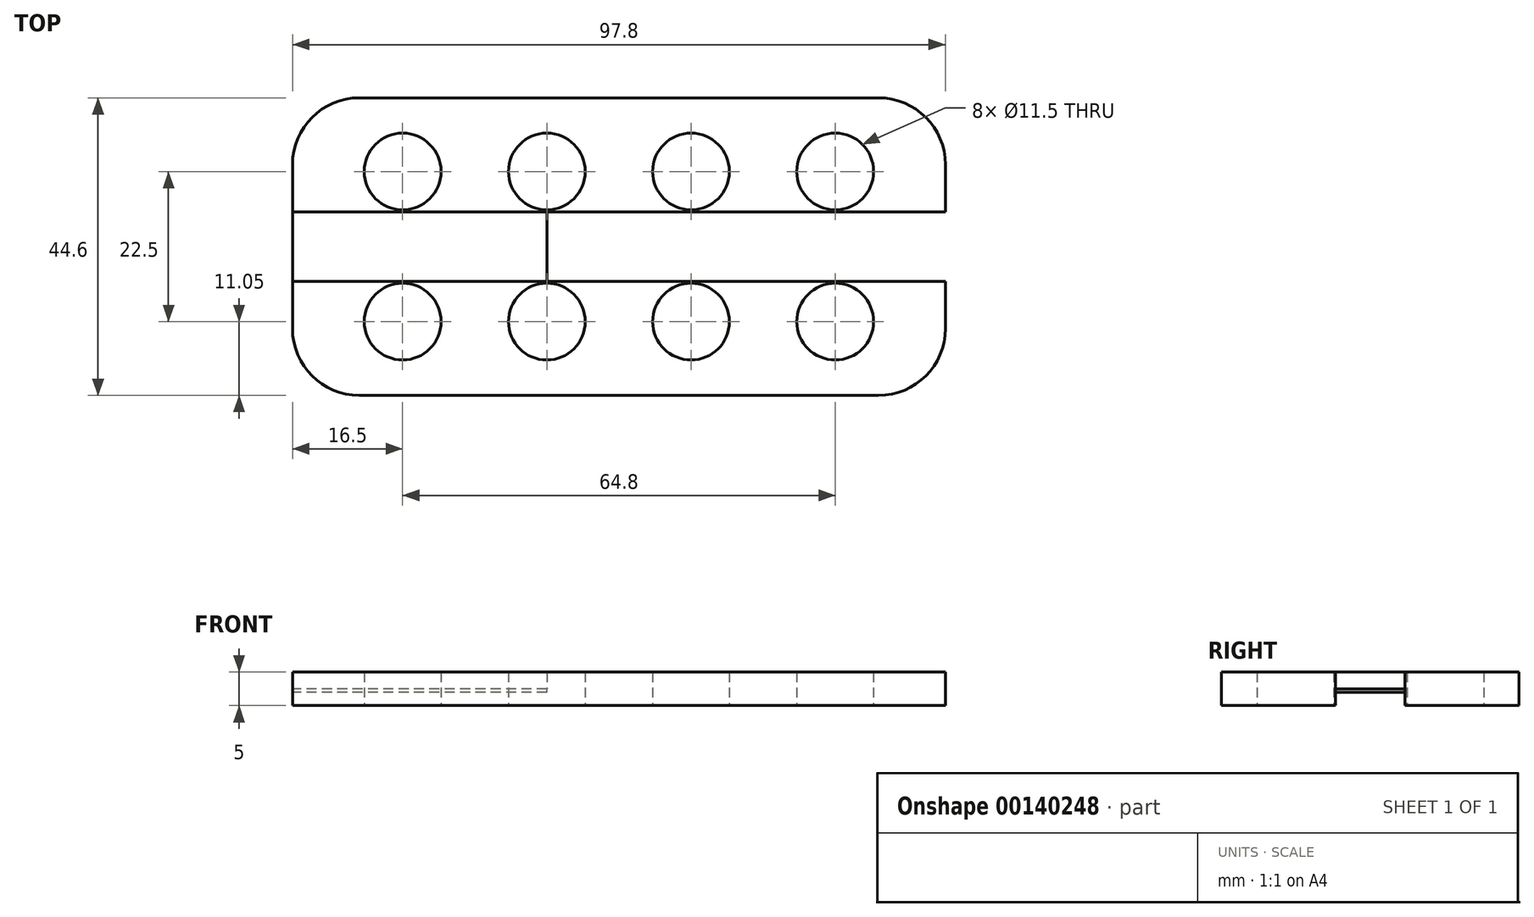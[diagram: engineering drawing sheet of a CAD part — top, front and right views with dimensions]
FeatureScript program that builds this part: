
annotation { "Feature Type Name" : "Feature", "Feature Type Description" : "" }
export const myFeature = defineFeature(function(context is Context, id is Id, definition is map)
    precondition{}
    {
        {
            var Q0;
            Q0=qCreatedBy(makeId("Top.planeOp"),FACE);
            var sketch = newSketch(context, id + "F0", { "sketchPlane" : qUnion([Q0])});
            skLineSegment(sketch, "E0", {"start": v(-3.6, 0) * mm, "end": v(-3.6, 10.25) * mm});
            skLineSegment(sketch, "E1", {"start": v(-3.6, 10.25) * mm, "end": v(18, 10.25) * mm});
            skLineSegment(sketch, "E2", {"start": v(-3.6, 10.25) * mm, "end": v(-25.2, 10.25) * mm});
            skLineSegment(sketch, "E3", {"start": v(-3.6, 0) * mm, "end": v(-3.6, -10.25) * mm});
            skLineSegment(sketch, "E4", {"start": v(-3.6, -10.25) * mm, "end": v(-25.2, -10.25) * mm});
            skLineSegment(sketch, "E5", {"start": v(-3.6, -10.25) * mm, "end": v(18, -10.25) * mm});
            skLineSegment(sketch, "E6.0", {"start": v(-3.6, 11.25) * mm, "end": v(-25.2, 11.25) * mm});
            skLineSegment(sketch, "E6.1", {"start": v(-3.6, 11.25) * mm, "end": v(18, 11.25) * mm});
            skLineSegment(sketch, "E7.0", {"start": v(-3.6, -11.25) * mm, "end": v(18, -11.25) * mm});
            skLineSegment(sketch, "E7.1", {"start": v(-3.6, -11.25) * mm, "end": v(-25.2, -11.25) * mm});
            skLineSegment(sketch, "E8", {"start": v(18, -11.25) * mm, "end": v(39.6, -11.25) * mm});
            skLineSegment(sketch, "E9", {"start": v(18, 11.25) * mm, "end": v(39.6, 11.25) * mm});
            skLineSegment(sketch, "E10", {"start": v(7.2, 11.25) * mm, "end": v(7.2, 0) * mm});
            skLineSegment(sketch, "E11.bottom", {"start": v(-41.7, 22.3) * mm, "end": v(56.1, 22.3) * mm});
            skLineSegment(sketch, "E11.top", {"start": v(-41.7, -22.3) * mm, "end": v(56.1, -22.3) * mm});
            skLineSegment(sketch, "E11.left", {"start": v(-41.7, 22.3) * mm, "end": v(-41.7, -22.3) * mm});
            skLineSegment(sketch, "E11.right", {"start": v(56.1, 22.3) * mm, "end": v(56.1, -22.3) * mm});
            skPoint(sketch, "E11.middle", {"position": v(7.2, 0) * mm});
            skCircle(sketch, "E12", {"center": v(-25.2, 11.25) * mm, "radius": 5.75 * mm});
            skCircle(sketch, "E13", {"center": v(-3.6, 11.25) * mm, "radius": 5.75 * mm});
            skCircle(sketch, "E14", {"center": v(18, 11.25) * mm, "radius": 5.75 * mm});
            skCircle(sketch, "E15", {"center": v(39.6, 11.25) * mm, "radius": 5.75 * mm});
            skCircle(sketch, "E16", {"center": v(-25.2, -11.25) * mm, "radius": 5.75 * mm});
            skCircle(sketch, "E17", {"center": v(-3.6, -11.25) * mm, "radius": 5.75 * mm});
            skCircle(sketch, "E18", {"center": v(18, -11.25) * mm, "radius": 5.75 * mm});
            skCircle(sketch, "E19", {"center": v(39.6, -11.25) * mm, "radius": 5.75 * mm});
            skLineSegment(sketch, "E20", {"start": v(56.1, 0) * mm, "end": v(56.1, -5.2) * mm});
            skLineSegment(sketch, "E21", {"start": v(56.1, 0) * mm, "end": v(56.1, 5.2) * mm});
            skLineSegment(sketch, "E22", {"start": v(56.1, 5.2) * mm, "end": v(-41.7, 5.2) * mm});
            skLineSegment(sketch, "E23", {"start": v(56.1, -5.2) * mm, "end": v(-41.7, -5.2) * mm});
            skSolve(sketch);
        }
        {
            var Q0;
            Q0=makeQuery(id+"F0.imprint","IMPRINT",FACE,{"disambiguationData":[TD([[makeQuery(id+"F0.imprint","IMPRINT",EDGE,{"derivedFrom":sQuery(id+"F0.wireOp",EDGE,"E11.bottom")}),-1.0]])]});
            var Q1;
            {var subQ0=sQuery(id+"F0.wireOp",EDGE,"f6887ee9-049f-47f7-8b07-7ff9263f95ff");var subQ1=makeQuery(id+"F0.imprint","INTERSECT",VERTEX,{"derivedFrom":[sQuery(id+"F0.wireOp",EDGE,"E4"),subQ0]});Q1=makeQuery(id+"F0.imprint","IMPRINT",FACE,{"disambiguationData":[TD([[makeQuery(id+"F0.imprint","IMPRINT",EDGE,{"disambiguationData":[TD([[subQ1,-1.0]])],"derivedFrom":subQ0}),1.0]])]});}
            var Q2;
            {var subQ0=sQuery(id+"F0.wireOp",EDGE,"7b2065db-7b24-4620-b89c-c6dd7d309109");var subQ1=makeQuery(id+"F0.imprint","INTERSECT",VERTEX,{"derivedFrom":[sQuery(id+"F0.wireOp",EDGE,"E2"),subQ0]});Q2=makeQuery(id+"F0.imprint","IMPRINT",FACE,{"disambiguationData":[TD([[makeQuery(id+"F0.imprint","IMPRINT",EDGE,{"disambiguationData":[TD([[subQ1,-1.0]])],"derivedFrom":subQ0}),1.0]])]});}
            var Q3;
            {var subQ1=sQuery(id+"F0.wireOp",EDGE,"E0");var subQ3=sQuery(id+"F0.wireOp",EDGE,"3ee279bb-5b09-4dd3-93a1-242deb24ec6a");var subQ4=makeQuery(id+"F0.imprint","INTERSECT",VERTEX,{"derivedFrom":[subQ1,subQ3]});Q3=makeQuery(id+"F0.imprint","IMPRINT",FACE,{"disambiguationData":[TD([[makeQuery(id+"F0.imprint","IMPRINT",EDGE,{"disambiguationData":[TD([[subQ4,1.0]])],"derivedFrom":subQ3}),1.0]])]});}
            var Q4;
            {var subQ0=sQuery(id+"F0.wireOp",EDGE,"4c88f515-e4cd-4761-96bb-9e012f7b4129");var subQ1=makeQuery(id+"F0.imprint","INTERSECT",VERTEX,{"derivedFrom":[sQuery(id+"F0.wireOp",EDGE,"E1"),subQ0]});Q4=makeQuery(id+"F0.imprint","IMPRINT",FACE,{"disambiguationData":[TD([[makeQuery(id+"F0.imprint","IMPRINT",EDGE,{"disambiguationData":[TD([[subQ1,1.0]])],"derivedFrom":subQ0}),1.0]])]});}
            var Q5;
            {var subQ0=sQuery(id+"F0.wireOp",EDGE,"98f43cb8-49ac-4cd2-891b-843e99cd508c");var subQ1=makeQuery(id+"F0.imprint","INTERSECT",VERTEX,{"derivedFrom":[sQuery(id+"F0.wireOp",EDGE,"E5"),subQ0]});Q5=makeQuery(id+"F0.imprint","IMPRINT",FACE,{"disambiguationData":[TD([[makeQuery(id+"F0.imprint","IMPRINT",EDGE,{"disambiguationData":[TD([[subQ1,-1.0]])],"derivedFrom":subQ0}),1.0]])]});}
            var Q6;
            {var subQ1=sQuery(id+"F0.wireOp",EDGE,"E0");var subQ3=sQuery(id+"F0.wireOp",EDGE,"3ee279bb-5b09-4dd3-93a1-242deb24ec6a");var subQ4=makeQuery(id+"F0.imprint","INTERSECT",VERTEX,{"derivedFrom":[subQ1,subQ3]});Q6=makeQuery(id+"F0.imprint","IMPRINT",FACE,{"disambiguationData":[TD([[makeQuery(id+"F0.imprint","IMPRINT",EDGE,{"disambiguationData":[TD([[subQ4,-1.0]])],"derivedFrom":subQ3}),1.0]])]});}
            var Q7;
            {var subQ3=sQuery(id+"F0.wireOp",EDGE,"3ee279bb-5b09-4dd3-93a1-242deb24ec6a");var subQ5=sQuery(id+"F0.wireOp",EDGE,"E6.1");var subQ8=makeQuery(id+"F0.imprint","INTERSECT",VERTEX,{"derivedFrom":[subQ3,subQ5]});Q7=makeQuery(id+"F0.imprint","IMPRINT",FACE,{"disambiguationData":[TD([[makeQuery(id+"F0.imprint","IMPRINT",EDGE,{"disambiguationData":[TD([[subQ8,1.0]])],"derivedFrom":subQ3}),1.0]])]});}
            var Q8;
            {var subQ0=sQuery(id+"F0.wireOp",EDGE,"E6.1");var subQ1=sQuery(id+"F0.wireOp",EDGE,"3ee279bb-5b09-4dd3-93a1-242deb24ec6a");var subQ2=makeQuery(id+"F0.imprint","INTERSECT",VERTEX,{"derivedFrom":[subQ1,subQ0]});Q8=makeQuery(id+"F0.imprint","IMPRINT",FACE,{"disambiguationData":[TD([[makeQuery(id+"F0.imprint","IMPRINT",EDGE,{"disambiguationData":[TD([[subQ2,-1.0]])],"derivedFrom":subQ1}),1.0]])]});}
            var Q9;
            {var subQ0=sQuery(id+"F0.wireOp",EDGE,"E9");var subQ1=sQuery(id+"F0.wireOp",EDGE,"4c88f515-e4cd-4761-96bb-9e012f7b4129");var subQ2=makeQuery(id+"F0.imprint","INTERSECT",VERTEX,{"derivedFrom":[subQ1,subQ0]});Q9=makeQuery(id+"F0.imprint","IMPRINT",FACE,{"disambiguationData":[TD([[makeQuery(id+"F0.imprint","IMPRINT",EDGE,{"disambiguationData":[TD([[subQ2,-1.0]])],"derivedFrom":subQ1}),1.0]])]});}
            var Q10;
            {var subQ0=sQuery(id+"F0.wireOp",EDGE,"E7.1");var subQ1=sQuery(id+"F0.wireOp",EDGE,"78d3df8a-ec91-46e3-93df-5ccd42c28f7d");var subQ2=makeQuery(id+"F0.imprint","INTERSECT",VERTEX,{"derivedFrom":[subQ1,subQ0]});Q10=makeQuery(id+"F0.imprint","IMPRINT",FACE,{"disambiguationData":[TD([[makeQuery(id+"F0.imprint","IMPRINT",EDGE,{"disambiguationData":[TD([[subQ2,-1.0]])],"derivedFrom":subQ1}),1.0]])]});}
            var Q11;
            {var subQ0=sQuery(id+"F0.wireOp",EDGE,"E8");var subQ1=sQuery(id+"F0.wireOp",EDGE,"98f43cb8-49ac-4cd2-891b-843e99cd508c");var subQ2=makeQuery(id+"F0.imprint","INTERSECT",VERTEX,{"derivedFrom":[subQ1,subQ0]});Q11=makeQuery(id+"F0.imprint","IMPRINT",FACE,{"disambiguationData":[TD([[makeQuery(id+"F0.imprint","IMPRINT",EDGE,{"disambiguationData":[TD([[subQ2,1.0]])],"derivedFrom":subQ1}),1.0]])]});}
            var Q12;
            {var subQ0=sQuery(id+"F0.wireOp",EDGE,"E10");var subQ1=sQuery(id+"F0.wireOp",EDGE,"E1");var subQ2=makeQuery(id+"F0.imprint","INTERSECT",VERTEX,{"derivedFrom":[subQ1,subQ0]});Q12=makeQuery(id+"F0.imprint","IMPRINT",FACE,{"disambiguationData":[TD([[makeQuery(id+"F0.imprint","IMPRINT",EDGE,{"disambiguationData":[TD([[subQ2,-1.0]])],"derivedFrom":subQ1}),1.0]])]});}
            var Q13;
            {var subQ1=sQuery(id+"F0.wireOp",EDGE,"E3");var subQ3=sQuery(id+"F0.wireOp",EDGE,"78d3df8a-ec91-46e3-93df-5ccd42c28f7d");var subQ4=makeQuery(id+"F0.imprint","INTERSECT",VERTEX,{"derivedFrom":[subQ1,subQ3]});Q13=makeQuery(id+"F0.imprint","IMPRINT",FACE,{"disambiguationData":[TD([[makeQuery(id+"F0.imprint","IMPRINT",EDGE,{"disambiguationData":[TD([[subQ4,-1.0]])],"derivedFrom":subQ3}),1.0]])]});}
            var Q14;
            {var subQ0=sQuery(id+"F0.wireOp",EDGE,"E10");var subQ1=sQuery(id+"F0.wireOp",EDGE,"E1");var subQ2=makeQuery(id+"F0.imprint","INTERSECT",VERTEX,{"derivedFrom":[subQ1,subQ0]});Q14=makeQuery(id+"F0.imprint","IMPRINT",FACE,{"disambiguationData":[TD([[makeQuery(id+"F0.imprint","IMPRINT",EDGE,{"disambiguationData":[TD([[subQ2,-1.0]])],"derivedFrom":subQ1}),1.0]])]});}
            var Q15;
            {var subQ0=sQuery(id+"F0.wireOp",EDGE,"E6.1");var subQ1=sQuery(id+"F0.wireOp",EDGE,"3ee279bb-5b09-4dd3-93a1-242deb24ec6a");var subQ2=makeQuery(id+"F0.imprint","INTERSECT",VERTEX,{"derivedFrom":[subQ1,subQ0]});Q15=makeQuery(id+"F0.imprint","IMPRINT",FACE,{"disambiguationData":[TD([[makeQuery(id+"F0.imprint","IMPRINT",EDGE,{"disambiguationData":[TD([[subQ2,1.0]])],"derivedFrom":subQ1}),-1.0]])]});}
            var Q16;
            {var subQ0=sQuery(id+"F0.wireOp",EDGE,"E6.0");var subQ1=sQuery(id+"F0.wireOp",EDGE,"3ee279bb-5b09-4dd3-93a1-242deb24ec6a");var subQ2=makeQuery(id+"F0.imprint","INTERSECT",VERTEX,{"derivedFrom":[subQ1,subQ0]});Q16=makeQuery(id+"F0.imprint","IMPRINT",FACE,{"disambiguationData":[TD([[makeQuery(id+"F0.imprint","IMPRINT",EDGE,{"disambiguationData":[TD([[subQ2,-1.0]])],"derivedFrom":subQ1}),-1.0]])]});}
            var Q17;
            {var subQ0=sQuery(id+"F0.wireOp",EDGE,"f6887ee9-049f-47f7-8b07-7ff9263f95ff");var subQ1=sQuery(id+"F0.wireOp",EDGE,"E4");var subQ2=makeQuery(id+"F0.imprint","INTERSECT",VERTEX,{"derivedFrom":[subQ1,subQ0]});Q17=makeQuery(id+"F0.imprint","IMPRINT",FACE,{"disambiguationData":[TD([[makeQuery(id+"F0.imprint","IMPRINT",EDGE,{"disambiguationData":[TD([[subQ2,1.0]])],"derivedFrom":subQ1}),1.0]])]});}
            var Q18;
            {var subQ1=sQuery(id+"F0.wireOp",EDGE,"E3");var subQ3=sQuery(id+"F0.wireOp",EDGE,"78d3df8a-ec91-46e3-93df-5ccd42c28f7d");var subQ4=makeQuery(id+"F0.imprint","INTERSECT",VERTEX,{"derivedFrom":[subQ1,subQ3]});Q18=makeQuery(id+"F0.imprint","IMPRINT",FACE,{"disambiguationData":[TD([[makeQuery(id+"F0.imprint","IMPRINT",EDGE,{"disambiguationData":[TD([[subQ4,1.0]])],"derivedFrom":subQ3}),1.0]])]});}
            var Q19;
            {var subQ0=sQuery(id+"F0.wireOp",EDGE,"78d3df8a-ec91-46e3-93df-5ccd42c28f7d");var subQ5=sQuery(id+"F0.wireOp",EDGE,"E4");var subQ6=makeQuery(id+"F0.imprint","INTERSECT",VERTEX,{"derivedFrom":[subQ5,subQ0]});Q19=makeQuery(id+"F0.imprint","IMPRINT",FACE,{"disambiguationData":[TD([[makeQuery(id+"F0.imprint","IMPRINT",EDGE,{"disambiguationData":[TD([[subQ6,-1.0]])],"derivedFrom":subQ0}),1.0]])]});}
            var Q20;
            {var subQ0=sQuery(id+"F0.wireOp",EDGE,"98f43cb8-49ac-4cd2-891b-843e99cd508c");var subQ1=sQuery(id+"F0.wireOp",EDGE,"E5");var subQ2=makeQuery(id+"F0.imprint","INTERSECT",VERTEX,{"derivedFrom":[subQ1,subQ0]});Q20=makeQuery(id+"F0.imprint","IMPRINT",FACE,{"disambiguationData":[TD([[makeQuery(id+"F0.imprint","IMPRINT",EDGE,{"disambiguationData":[TD([[subQ2,1.0]])],"derivedFrom":subQ1}),-1.0]])]});}
            var Q21;
            {var subQ0=sQuery(id+"F0.wireOp",EDGE,"E10");var subQ1=sQuery(id+"F0.wireOp",EDGE,"E1");var subQ2=makeQuery(id+"F0.imprint","INTERSECT",VERTEX,{"derivedFrom":[subQ1,subQ0]});Q21=makeQuery(id+"F0.imprint","IMPRINT",FACE,{"disambiguationData":[TD([[makeQuery(id+"F0.imprint","IMPRINT",EDGE,{"disambiguationData":[TD([[subQ2,1.0]])],"derivedFrom":subQ1}),1.0]])]});}
            var Q22;
            {var subQ0=sQuery(id+"F0.wireOp",EDGE,"E12");var subQ1=sQuery(id+"F0.wireOp",EDGE,"E2");var subQ2=makeQuery(id+"F0.imprint","INTERSECT",VERTEX,{"derivedFrom":[subQ1,subQ0]});Q22=makeQuery(id+"F0.imprint","IMPRINT",FACE,{"disambiguationData":[TD([[makeQuery(id+"F0.imprint","IMPRINT",EDGE,{"disambiguationData":[TD([[subQ2,1.0]])],"derivedFrom":subQ1}),-1.0]])]});}
            var Q23;
            {var subQ8=sQuery(id+"F0.wireOp",EDGE,"E11.top");Q23=makeQuery(id+"F0.imprint","IMPRINT",FACE,{"disambiguationData":[TD([[makeQuery(id+"F0.imprint","IMPRINT",EDGE,{"derivedFrom":subQ8}),1.0]])]});}
            var Q24;
            {var subQ1=sQuery(id+"F0.wireOp",EDGE,"E0");var subQ5=sQuery(id+"F0.wireOp",EDGE,"E22");var subQ9=makeQuery(id+"F0.imprint","INTERSECT",VERTEX,{"derivedFrom":[subQ1,subQ5]});Q24=makeQuery(id+"F0.imprint","IMPRINT",FACE,{"disambiguationData":[TD([[makeQuery(id+"F0.imprint","IMPRINT",EDGE,{"disambiguationData":[TD([[subQ9,-1.0]])],"derivedFrom":subQ1}),-1.0]])]});}
            extrude(context, id + "F1", {"entities" : qUnion([Q0, Q1, Q2, Q3, Q4, Q5, Q6, Q7, Q8, Q9, Q10, Q11, Q12, Q13, Q14, Q15, Q16, Q17, Q18, Q19, Q20, Q21, Q22, Q23, Q24]), "endBound" : BoundingType.SYMMETRIC, "depth" : 5 * mm});
        }
        {
            var Q0;
            {var subQ3=sQuery(id+"F0.wireOp",EDGE,"E0");var subQ5=sQuery(id+"F0.wireOp",EDGE,"E3");var subQ6=makeQuery(id+"F0.imprint","INTERSECT",VERTEX,{"derivedFrom":[subQ3,subQ5]});Q0=makeQuery(id+"F0.imprint","IMPRINT",FACE,{"disambiguationData":[TD([[makeQuery(id+"F0.imprint","IMPRINT",EDGE,{"disambiguationData":[TD([[subQ6,-1.0]])],"derivedFrom":subQ3}),1.0]])]});}
            var Q1;
            {var subQ6=sQuery(id+"F0.wireOp",EDGE,"E20");Q1=makeQuery(id+"F0.imprint","IMPRINT",FACE,{"disambiguationData":[TD([[makeQuery(id+"F0.imprint","IMPRINT",EDGE,{"derivedFrom":subQ6}),-1.0]])]});}
            extrude(context, id + "F2", {"entities" : qUnion([Q0, Q1]), "depth" : 2.5 * mm});
        }
        {
            var Q0;
            {var subQ6=sQuery(id+"F0.wireOp",EDGE,"E20");Q0=makeQuery(id+"F0.imprint","IMPRINT",FACE,{"disambiguationData":[TD([[makeQuery(id+"F0.imprint","IMPRINT",EDGE,{"derivedFrom":subQ6}),-1.0]])]});}
            var Q1;
            {var subQ3=sQuery(id+"F0.wireOp",EDGE,"E0");var subQ5=sQuery(id+"F0.wireOp",EDGE,"E3");var subQ6=makeQuery(id+"F0.imprint","INTERSECT",VERTEX,{"derivedFrom":[subQ3,subQ5]});Q1=makeQuery(id+"F0.imprint","IMPRINT",FACE,{"disambiguationData":[TD([[makeQuery(id+"F0.imprint","IMPRINT",EDGE,{"disambiguationData":[TD([[subQ6,-1.0]])],"derivedFrom":subQ3}),1.0]])]});}
            extrude(context, id + "F3", {"entities" : qUnion([Q0, Q1]), "oppositeDirection" : true, "depth" : 0.5 * mm});
        }
        {
            var Q0;
            Q0=makeQuery(id+"F1.opExtrude","SWEPT_EDGE",EDGE,{"disambiguationData":[OSD([sQuery(id+"F0.wireOp",EDGE,"E11.top"),sQuery(id+"F0.wireOp",EDGE,"E11.right")])]});
            var Q1;
            Q1=makeQuery(id+"F1.opExtrude","SWEPT_EDGE",EDGE,{"disambiguationData":[OSD([sQuery(id+"F0.wireOp",EDGE,"E11.top"),sQuery(id+"F0.wireOp",EDGE,"E11.left")])]});
            var Q2;
            Q2=makeQuery(id+"F1.opExtrude","SWEPT_EDGE",EDGE,{"disambiguationData":[OSD([sQuery(id+"F0.wireOp",EDGE,"E11.bottom"),sQuery(id+"F0.wireOp",EDGE,"E11.left")])]});
            var Q3;
            Q3=makeQuery(id+"F1.opExtrude","SWEPT_EDGE",EDGE,{"disambiguationData":[OSD([sQuery(id+"F0.wireOp",EDGE,"E11.bottom"),sQuery(id+"F0.wireOp",EDGE,"E11.right")])]});
            fillet(context, id + "F4", {"entities" : qUnion([Q0, Q1, Q2, Q3]), "radius" : 10 * mm, "tangentPropagation" : true, "allowEdgeOverflow" : false});
        }
    });
